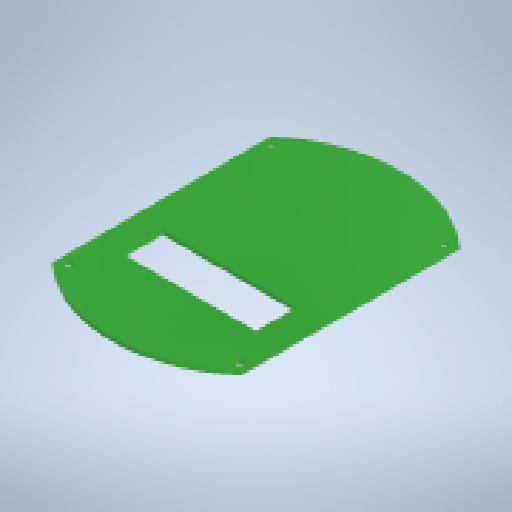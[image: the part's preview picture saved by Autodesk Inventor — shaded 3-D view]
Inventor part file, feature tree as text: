
AUTODESK INVENTOR PART (.ipt)
format: ipt  version: 2025.3 (Build 293356000, 356)  size: 160,768 bytes
history: native  units: mm
features: sketch x3, extrude x2, other x1, hole x1
ambient origin geometry x8: Origin, YZ Plane, XZ Plane, XY Plane, X Axis, Y Axis, Z Axis, Center Point
bodies: Body1 (feature_tree)
feature tree (7):
  other  "ソリッド1"
  extrude  "基板"  Depth=130.0mm
  hole  "スペーサ取付穴"  [1 undecoded]
  extrude  "バッテリー通し穴"  Depth=1.6mm TaperAngle=0.0deg
  sketch  "スケッチ1"
  sketch  "スケッチ4"
  sketch  "スケッチ5"
note: 1 required parameter value undecoded (feature->parameter linkage not recoverable at this tier; creation-order binding heuristic only, values carry confidence <= 0.55)
